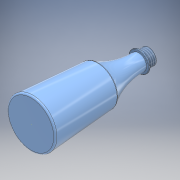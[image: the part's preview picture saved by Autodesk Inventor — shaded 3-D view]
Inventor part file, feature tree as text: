
AUTODESK INVENTOR PART (.ipt)
format: ipt  version: 2018 (Build 220112000, 112)  size: 232,448 bytes
history: native  units: mm
features: sketch x4, fillet x3, revolve x1, shell x1, thread x1
ambient origin geometry x8: Origin, YZ Plane, XZ Plane, XY Plane, X Axis, Y Axis, Z Axis, Center Point
bodies: Solid1 (feature_tree)
feature tree (10):
  revolve  "Revolution1"  [1 undecoded]
  shell  "Shell1"  Thickness=2.0mm
  fillet  "Fillet1"  Radius=2.0mm
  fillet  "Fillet2"  Radius=0.5mm
  fillet  "Fillet3"  Radius=10.0mm
  thread  "Thread1"  [1 undecoded]
  sketch  "3D Sketch1"
  sketch  "Sketch2"
  sketch  "Sketch3"
  sketch  "Sketch1"  dims[d1=90.0deg d2=1.0mm d3=2.0mm d4=2.0mm d5=0.5mm d6=10.0mm d7=0.0mm]
note: 2 required parameter values undecoded (feature->parameter linkage not recoverable at this tier; creation-order binding heuristic only, values carry confidence <= 0.55)